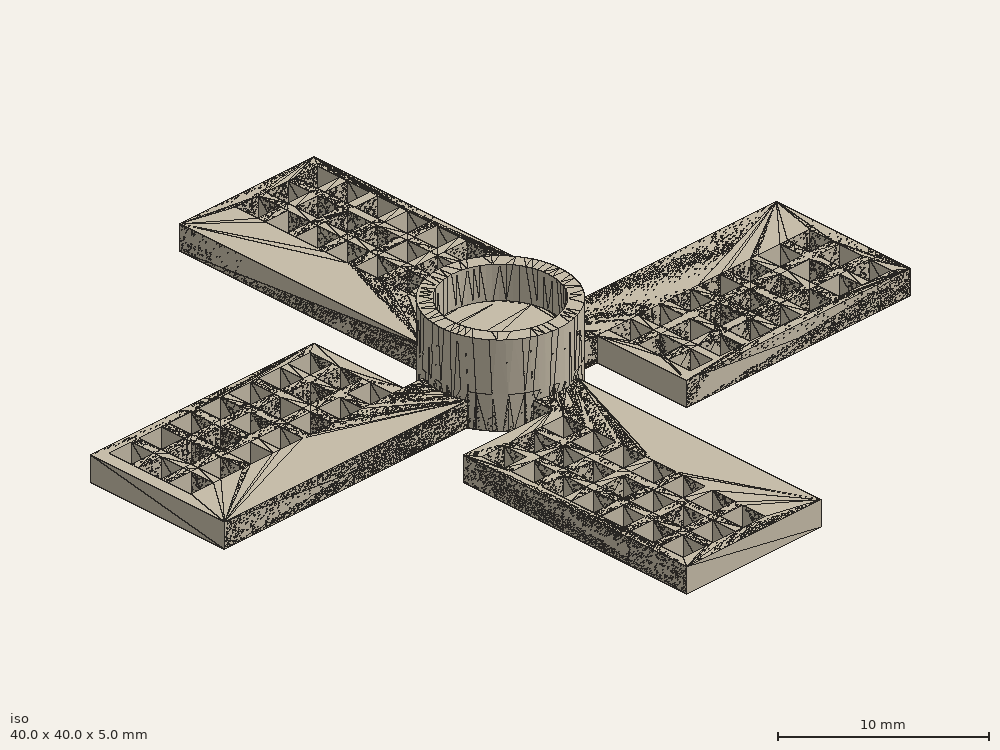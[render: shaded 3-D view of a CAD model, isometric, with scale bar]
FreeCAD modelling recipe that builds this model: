
FCSTD DOCUMENT  (FreeCAD 0.18R14555 (Git shallow))
Label: nema-17-windmill
License: All rights reserved
LicenseURL: http://en.wikipedia.org/wiki/All_rights_reserved
objects: Part::Cylinder×5, Part::Feature×3, Part::Cut×3, Part::MultiFuse×2, Mesh::Feature×1, Part::Chamfer×1
note: 14 computed .brp shape members not serialized (recipe doc carries the construction recipe); baked Part::Feature solids carry a one-line shape summary decoded from their .brp

FEATURE [Mesh::Feature] NEMA_Extruder_motor_rotation_indicator_Windmill_1_  label="NEMA_Extruder_motor_rotation_indicator_Windmill(1)"
FEATURE [Part::Feature] NEMA_Extruder_motor_rotation_indicator_Windmill_1_001
  Placement = pos=(48,-28,0) rot=(0,0,1;0rad)
  shape: bbox 40 x 40 x 2 mm, 2096 faces, 0 solids (baked)
FEATURE [Part::Cylinder] Cylinder
  Angle = 360
  AttacherType = Attacher::AttachEngine3D
  Height = 10
  Placement = pos=(0,0,2) rot=(0,0,1;0rad)
  Radius = 3.2
FEATURE [Part::Cylinder] Cylinder001
  Angle = 360
  AttacherType = Attacher::AttachEngine3D
  Height = 5
  Radius = 4
FEATURE [Part::Feature] NEMA_Extruder_motor_rotation_indicator_Windmill_1_001_solid  label="NEMA_Extruder_motor_rotation_indicator_Windmill_1_001 (Solid)"
  shape: bbox 40 x 40 x 2 mm, 2096 faces (baked)
FEATURE [Part::Cylinder] Cylinder002
  Angle = 360
  AttacherType = Attacher::AttachEngine3D
  Height = 2
  Placement = pos=(0,0,-6) rot=(0,0,1;0rad)
  Radius = 3.5
FEATURE [Part::Cylinder] Cylinder003
  Angle = 360
  AttacherType = Attacher::AttachEngine3D
  Height = 2
  Placement = pos=(0,0,-6) rot=(0,0,1;0rad)
  Radius = 2.5
FEATURE [Part::Cut] Cut001
  Base = -> Cylinder002
  Placement = pos=(0,0,-8) rot=(0,0,1;0rad)
  Tool = -> Cylinder003
FEATURE [Part::Chamfer] Chamfer
  Base = -> Cut001
  Edges = 1 edges r=0.9: [Edge1]
  Placement = pos=(0,0,13) rot=(0,0,1;0rad)
FEATURE [Part::Cut] Cut
  Base = -> Cylinder001
  Tool = -> Cylinder
FEATURE [Part::MultiFuse] Fusion
  Shapes = -> [NEMA_Extruder_motor_rotation_indicator_Windmill_1_001_solid,Cut]
FEATURE [Part::Cut] Cut002
  Base = -> Fusion
  Tool = -> Chamfer
FEATURE [Part::Cylinder] Cylinder004
  Angle = 360
  AttacherType = Attacher::AttachEngine3D
  Height = 1
  Placement = pos=(0,0,2) rot=(0,0,1;0rad)
  Radius = 3.5
FEATURE [Part::MultiFuse] Fusion001
  Shapes = -> [Cylinder004,Cut002]
FEATURE [Part::Feature] Fusion001001_solid  label="Fusion002 (Solid)"
  shape: bbox 40 x 40 x 5 mm, 509 faces (baked)
